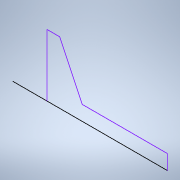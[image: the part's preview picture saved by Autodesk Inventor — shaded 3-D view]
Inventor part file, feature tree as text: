
AUTODESK INVENTOR PART (.ipt)
format: ipt  version: 2021 (Build 250183000, 183)  size: 84,992 bytes
history: native  units: mm
features: sketch x1
ambient origin geometry x8: Origin, YZ Plane, XZ Plane, XY Plane, X Axis, Y Axis, Z Axis, Center Point
feature tree (1):
  sketch  "Sketch1"
